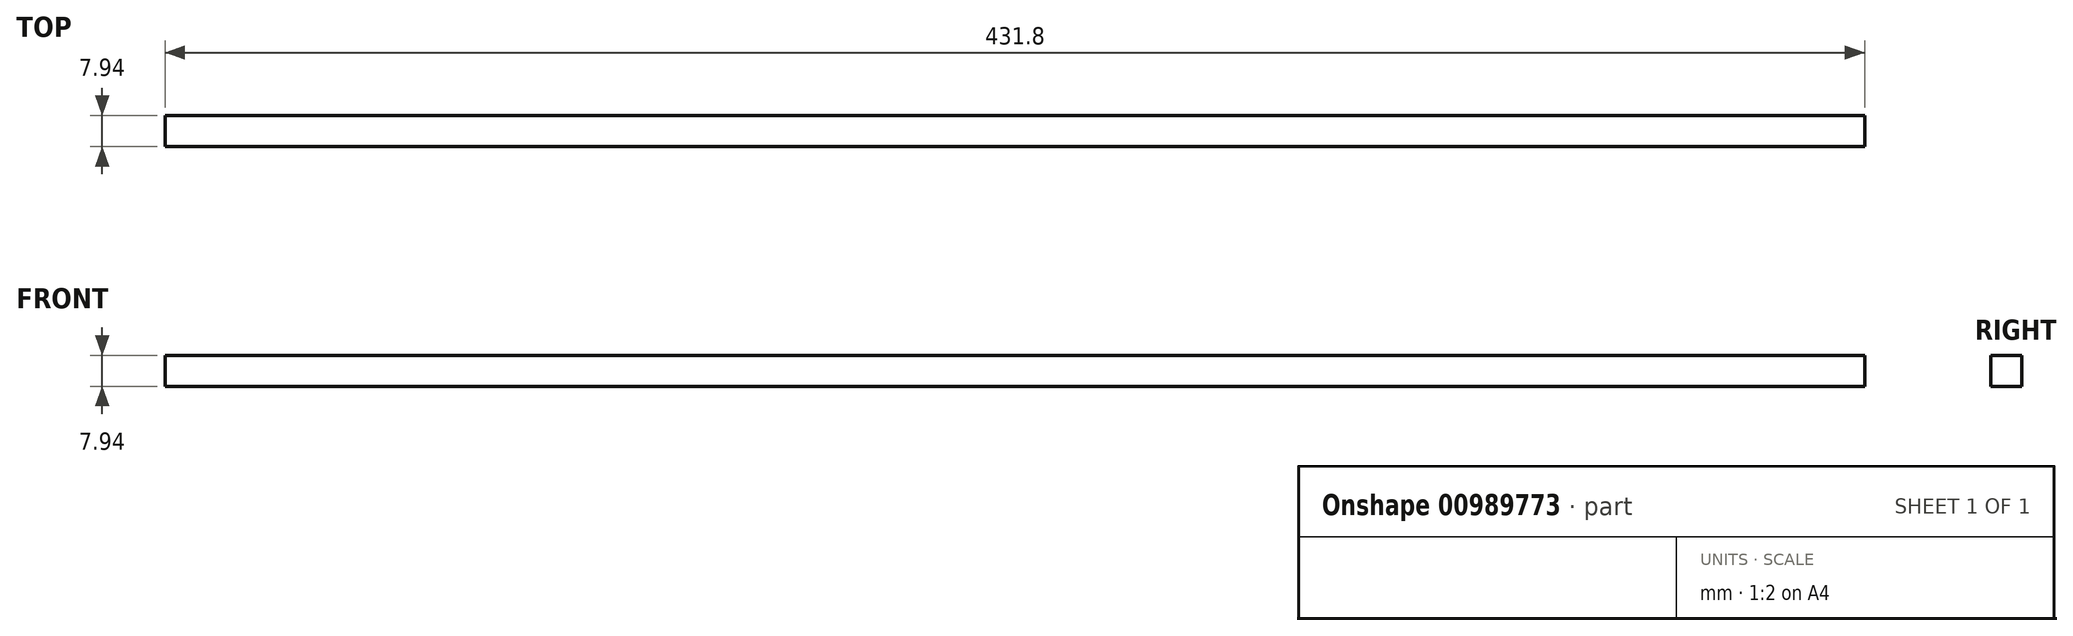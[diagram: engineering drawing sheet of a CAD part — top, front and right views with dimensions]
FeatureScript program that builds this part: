
annotation { "Feature Type Name" : "Feature", "Feature Type Description" : "" }
export const myFeature = defineFeature(function(context is Context, id is Id, definition is map)
    precondition{}
    {
        {
            var Q0;
            Q0=qCreatedBy(makeId("Right.planeOp"),FACE);
            var sketch = newSketch(context, id + "F0", { "sketchPlane" : qUnion([Q0])});
            skLineSegment(sketch, "E0.bottom", {"start": v(3.97, -3.97) * mm, "end": v(-3.97, -3.97) * mm});
            skLineSegment(sketch, "E0.top", {"start": v(3.97, 3.97) * mm, "end": v(-3.97, 3.97) * mm});
            skLineSegment(sketch, "E0.left", {"start": v(3.97, -3.97) * mm, "end": v(3.97, 3.97) * mm});
            skLineSegment(sketch, "E0.right", {"start": v(-3.97, -3.97) * mm, "end": v(-3.97, 3.97) * mm});
            skPoint(sketch, "E0.middle", {"position": v(0, 0) * mm});
            skSolve(sketch);
        }
        {
            var Q0;
            Q0=makeQuery(id+"F0.imprint","IMPRINT",FACE,{"disambiguationData":[TD([[makeQuery(id+"F0.imprint","IMPRINT",EDGE,{"derivedFrom":sQuery(id+"F0.wireOp",EDGE,"E0.bottom")}),-1.0]])]});
            extrude(context, id + "F1", {"entities" : qUnion([Q0]), "endBound" : BoundingType.SYMMETRIC, "depth" : 431.8 * mm, "offsetDistance" : 25.4 * mm});
        }
    });
